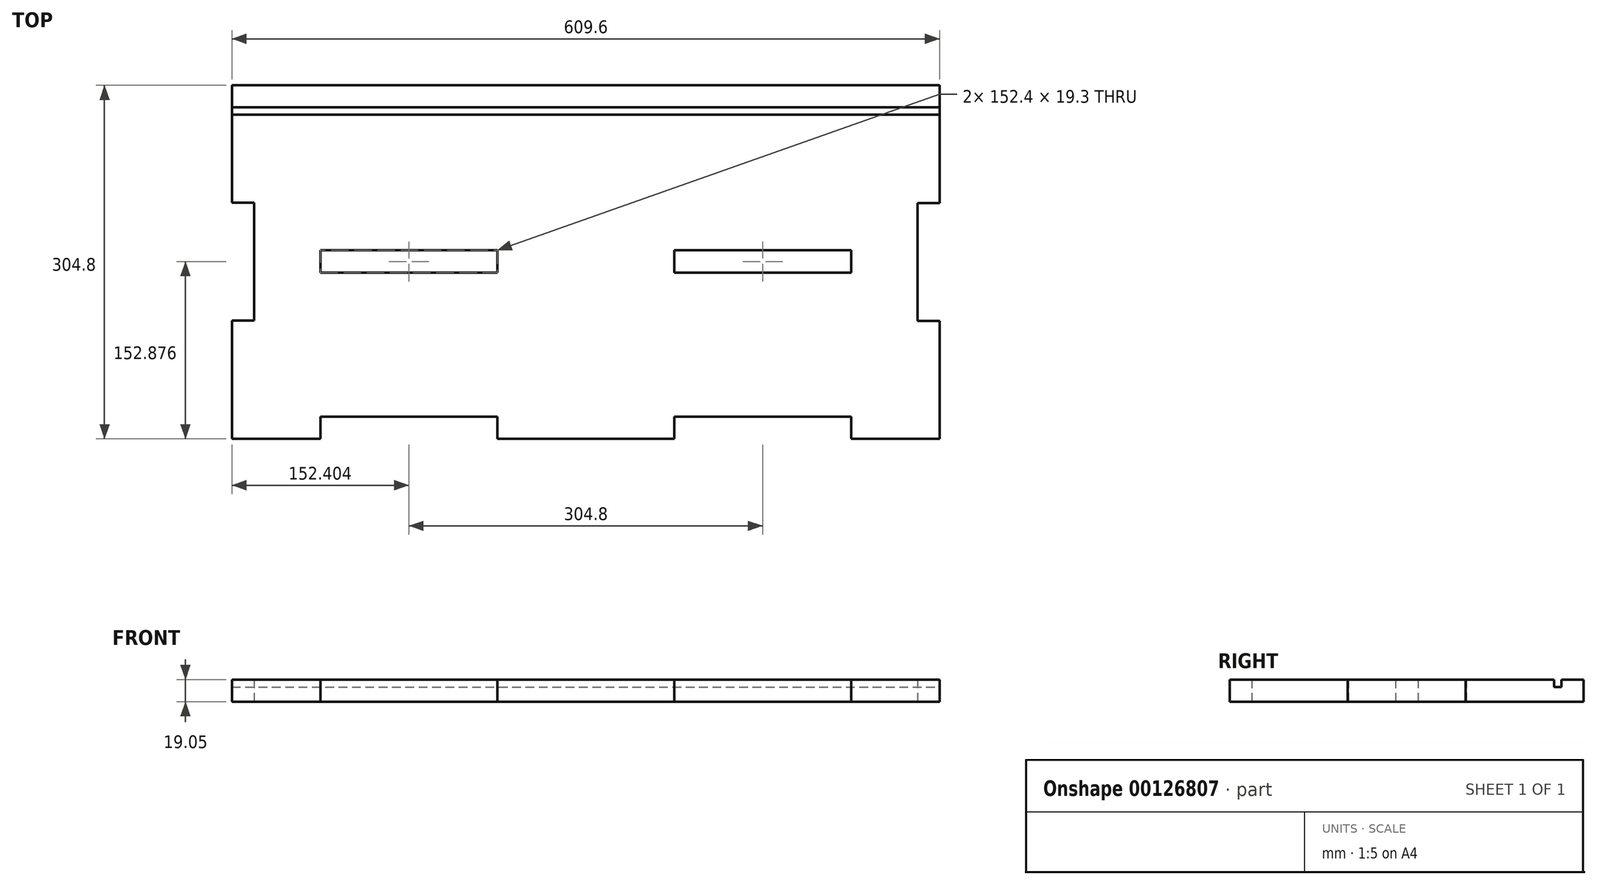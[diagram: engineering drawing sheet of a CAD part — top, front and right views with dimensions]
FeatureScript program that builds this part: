
annotation { "Feature Type Name" : "Feature", "Feature Type Description" : "" }
export const myFeature = defineFeature(function(context is Context, id is Id, definition is map)
    precondition{}
    {
        {
            var Q0;
            Q0=qCreatedBy(makeId("Top.planeOp"),FACE);
            var sketch = newSketch(context, id + "F0", { "sketchPlane" : qUnion([Q0])});
            skLineSegment(sketch, "E0.left", {"start": v(-234.96, 188.8) * mm, "end": v(-234.96, 87.68) * mm});
            skLineSegment(sketch, "E0.right", {"start": v(374.64, 188.8) * mm, "end": v(374.64, 87.2) * mm});
            skLineSegment(sketch, "E1.bottom", {"start": v(374.64, 188.8) * mm, "end": v(298.44, 188.8) * mm});
            skLineSegment(sketch, "E2.trimOffspring", {"start": v(298.44, 188.8) * mm, "end": v(374.64, 188.8) * mm});
            skLineSegment(sketch, "E3", {"start": v(-158.76, 188.8) * mm, "end": v(-234.96, 188.8) * mm});
            skPoint(sketch, "E4.end.orphan", {"position": v(-234.96, 36.4) * mm});
            skPoint(sketch, "E4.start.orphan", {"position": v(374.64, 36.4) * mm});
            skLineSegment(sketch, "E5.top", {"start": v(374.64, 87.2) * mm, "end": v(355.6, 87.2) * mm});
            skLineSegment(sketch, "E6", {"start": v(355.6, 87.2) * mm, "end": v(355.6, -14.4) * mm});
            skLineSegment(sketch, "E7", {"start": v(355.6, -14.4) * mm, "end": v(374.64, -14.4) * mm});
            skLineSegment(sketch, "E8.trimOffspring", {"start": v(374.64, -14.4) * mm, "end": v(374.64, -116) * mm});
            skLineSegment(sketch, "E9.MirrorCS", {"start": v(-234.96, 87.68) * mm, "end": v(-215.9, 87.68) * mm});
            skLineSegment(sketch, "E10.MirrorCS", {"start": v(-215.9, 87.68) * mm, "end": v(-215.9, -13.92) * mm});
            skLineSegment(sketch, "E11.MirrorCS", {"start": v(-215.9, -13.92) * mm, "end": v(-234.96, -13.92) * mm});
            skPoint(sketch, "E12.start.orphan", {"position": v(69.84, 188.8) * mm});
            skLineSegment(sketch, "E13.trimOffspring", {"start": v(-234.96, -13.92) * mm, "end": v(-234.96, -116) * mm});
            skLineSegment(sketch, "E14", {"start": v(-234.96, -116) * mm, "end": v(-158.76, -116) * mm});
            skLineSegment(sketch, "E15.0", {"start": v(298.44, -96.95) * mm, "end": v(146.04, -96.95) * mm});
            skLineSegment(sketch, "E16.0", {"start": v(-6.36, -96.95) * mm, "end": v(-158.76, -96.95) * mm});
            skLineSegment(sketch, "E17", {"start": v(-158.76, -96.95) * mm, "end": v(-158.76, -116) * mm});
            skLineSegment(sketch, "E18", {"start": v(-6.36, -96.95) * mm, "end": v(-6.36, -116) * mm});
            skLineSegment(sketch, "E19", {"start": v(146.04, -96.95) * mm, "end": v(146.04, -116) * mm});
            skLineSegment(sketch, "E20", {"start": v(298.44, -96.95) * mm, "end": v(298.44, -116) * mm});
            skLineSegment(sketch, "E21.trimOffspring", {"start": v(-6.36, -116) * mm, "end": v(146.04, -116) * mm});
            skLineSegment(sketch, "E22", {"start": v(298.44, -116) * mm, "end": v(374.64, -116) * mm});
            skLineSegment(sketch, "E23", {"start": v(-158.76, 188.8) * mm, "end": v(298.44, 188.8) * mm});
            skSolve(sketch);
        }
        {
            var Q0;
            Q0 = qSketchRegion(id + "F0", true);
            extrude(context, id + "F1", {"entities" : qUnion([Q0]), "depth" : 19.05 * mm});
        }
        {
            var Q0;
            Q0=makeQuery(id+"F1.opExtrude","CAP_FACE",FACE,{"disambiguationData":[OSD([sQuery(id+"F0.wireOp",EDGE,"E0.left"),sQuery(id+"F0.wireOp",EDGE,"E0.right"),sQuery(id+"F0.wireOp",EDGE,"E1.right"),sQuery(id+"F0.wireOp",EDGE,"E2.trimOffspring"),sQuery(id+"F0.wireOp",EDGE,"QrnToXiS-8W32-i9wu-8ZY2-wkroPjS9yFZF"),sQuery(id+"F0.wireOp",EDGE,"7CgUvwJA-YKIR-xiQ7-AEDa-8rmITTUws5iM"),sQuery(id+"F0.wireOp",EDGE,"Vaz8uSzH-i3Yl-YQJ0-aKDy-Y6cjIasddy4x"),sQuery(id+"F0.wireOp",EDGE,"nOBhDxEW-rfkv-9h7U-9Gz5-yhlAnRdpUGf9"),sQuery(id+"F0.wireOp",EDGE,"lYokkKIu-PkNV-shlm-j1yn-RVI2UM9GJehf"),sQuery(id+"F0.wireOp",EDGE,"UjU7FKxn-WVJg-odBu-ap1V-dYuEPOZ1TFnp"),sQuery(id+"F0.wireOp",EDGE,"E3"),sQuery(id+"F0.wireOp",EDGE,"E5.top"),sQuery(id+"F0.wireOp",EDGE,"E6"),sQuery(id+"F0.wireOp",EDGE,"E7"),sQuery(id+"F0.wireOp",EDGE,"E8.trimOffspring"),sQuery(id+"F0.wireOp",EDGE,"E9.MirrorCS"),sQuery(id+"F0.wireOp",EDGE,"E10.MirrorCS"),sQuery(id+"F0.wireOp",EDGE,"E11.MirrorCS"),sQuery(id+"F0.wireOp",EDGE,"E13.trimOffspring"),sQuery(id+"F0.wireOp",EDGE,"E14"),sQuery(id+"F0.wireOp",EDGE,"E15.0"),sQuery(id+"F0.wireOp",EDGE,"E16.0"),sQuery(id+"F0.wireOp",EDGE,"E17"),sQuery(id+"F0.wireOp",EDGE,"E18"),sQuery(id+"F0.wireOp",EDGE,"E19"),sQuery(id+"F0.wireOp",EDGE,"E20"),sQuery(id+"F0.wireOp",EDGE,"E21.trimOffspring"),sQuery(id+"F0.wireOp",EDGE,"E22")])],"isStart":false});
            var sketch = newSketch(context, id + "F2", { "sketchPlane" : qUnion([Q0])});
            skLineSegment(sketch, "E24.0", {"start": v(-158.76, 27.22) * mm, "end": v(-6.36, 27.22) * mm});
            skLineSegment(sketch, "E25.0", {"start": v(-158.76, 46.53) * mm, "end": v(-6.36, 46.53) * mm});
            skLineSegment(sketch, "E26", {"start": v(146.04, 46.53) * mm, "end": v(146.04, 27.22) * mm});
            skLineSegment(sketch, "E27", {"start": v(298.44, 46.53) * mm, "end": v(298.44, 27.22) * mm});
            skLineSegment(sketch, "E28", {"start": v(-6.36, 46.53) * mm, "end": v(-6.36, 27.22) * mm});
            skLineSegment(sketch, "E29", {"start": v(-158.76, 46.53) * mm, "end": v(-158.76, 27.22) * mm});
            skLineSegment(sketch, "E30.trimOffspring", {"start": v(146.04, 46.53) * mm, "end": v(298.44, 46.53) * mm});
            skLineSegment(sketch, "E31.trimOffspring", {"start": v(146.04, 27.22) * mm, "end": v(298.44, 27.22) * mm});
            skLineSegment(sketch, "E32", {"start": v(146.04, 27.22) * mm, "end": v(146.04, -96.95) * mm});
            skLineSegment(sketch, "E33", {"start": v(146.04, 46.53) * mm, "end": v(146.04, 188.8) * mm});
            skSolve(sketch);
        }
        {
            var Q0;
            Q0 = qSketchRegion(id + "F2", true);
            extrude(context, id + "F3", {"entities" : qUnion([Q0]), "operationType" : NewBodyOperationType.REMOVE, "endBound" : BoundingType.THROUGH_ALL, "oppositeDirection" : true, "depth" : 25.4 * mm});
        }
        {
            var Q0;
            Q0=makeQuery(id+"F1.opExtrude","SWEPT_FACE",FACE,{"disambiguationData":[OSD([sQuery(id+"F0.wireOp",EDGE,"E0.right")])]});
            var sketch = newSketch(context, id + "F4", { "sketchPlane" : qUnion([Q0])});
            skLineSegment(sketch, "E34.0", {"start": v(169.75, 19.05) * mm, "end": v(169.75, 12.7) * mm});
            skLineSegment(sketch, "E35.0", {"start": v(163.4, 19.05) * mm, "end": v(163.4, 12.7) * mm});
            skLineSegment(sketch, "E36", {"start": v(163.4, 19.05) * mm, "end": v(169.75, 19.05) * mm});
            skLineSegment(sketch, "E37.0", {"start": v(163.4, 12.7) * mm, "end": v(169.75, 12.7) * mm});
            skSolve(sketch);
        }
        {
            var Q0;
            Q0 = qSketchRegion(id + "F4", true);
            extrude(context, id + "F5", {"entities" : qUnion([Q0]), "operationType" : NewBodyOperationType.REMOVE, "endBound" : BoundingType.THROUGH_ALL, "oppositeDirection" : true, "depth" : 25.4 * mm});
        }
    });
